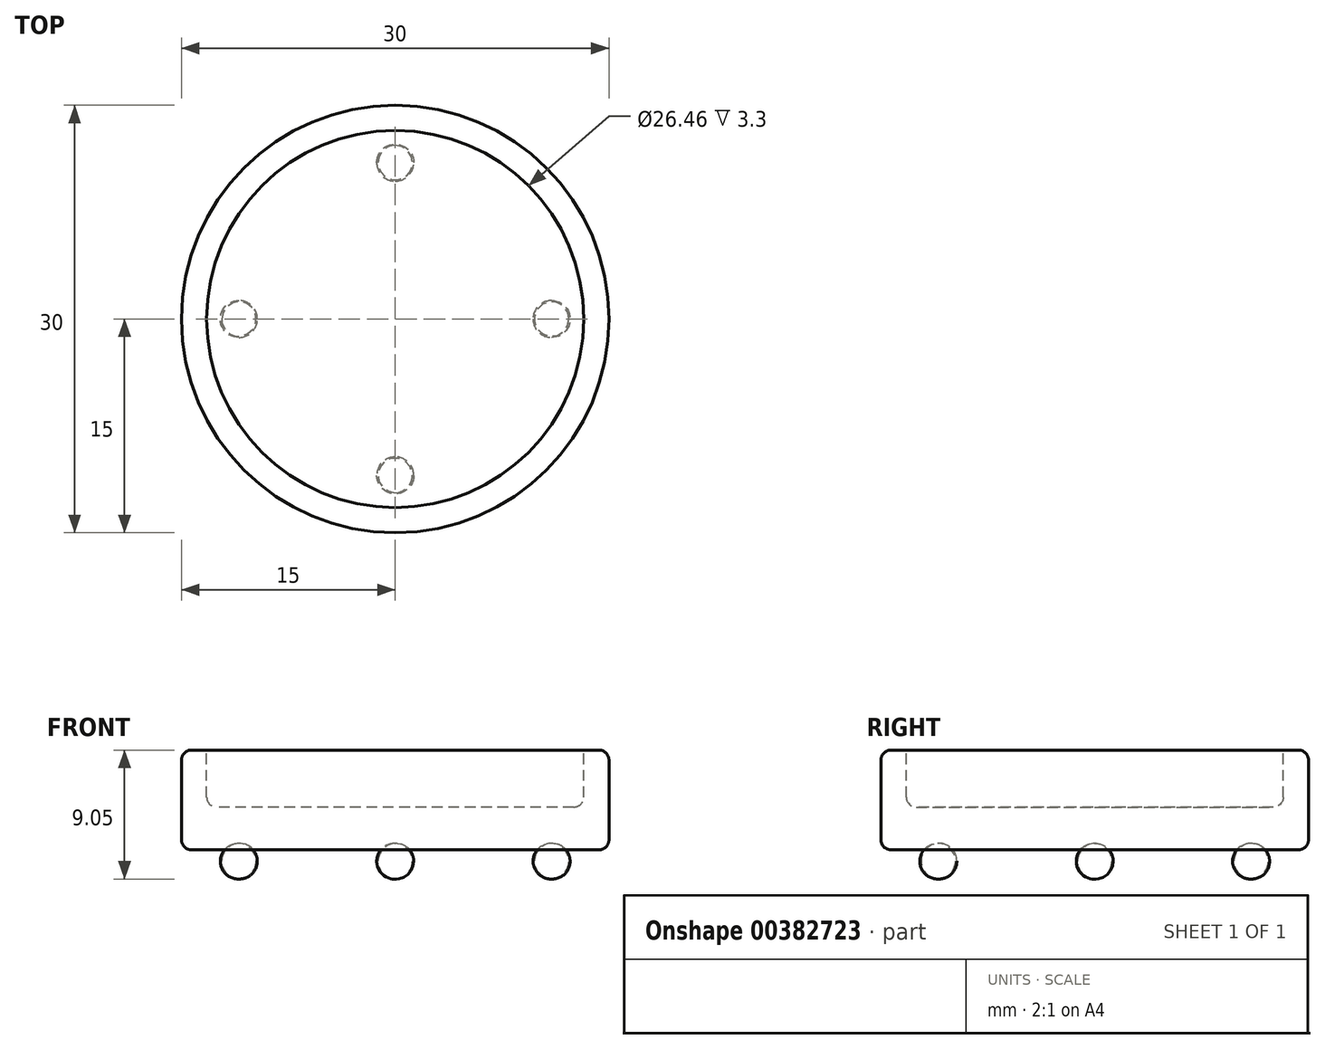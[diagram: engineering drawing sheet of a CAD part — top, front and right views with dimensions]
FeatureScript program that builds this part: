
annotation { "Feature Type Name" : "Feature", "Feature Type Description" : "" }
export const myFeature = defineFeature(function(context is Context, id is Id, definition is map)
    precondition{}
    {
        {
            var Q0;
            Q0=qCreatedBy(makeId("Top.planeOp"),FACE);
            var sketch = newSketch(context, id + "F0", { "sketchPlane" : qUnion([Q0])});
            skCircle(sketch, "E0", {"center": v(0, 0) * mm, "radius": 15 * mm});
            skSolve(sketch);
        }
        {
            var Q0;
            Q0 = qSketchRegion(id + "F0", true);
            extrude(context, id + "F1", {"entities" : qUnion([Q0]), "depth" : 7 * mm});
        }
        {
            var Q0;
            Q0=makeQuery(id+"F1.opExtrude","CAP_FACE",FACE,{"disambiguationData":[OSD([sQuery(id+"F0.wireOp",EDGE,"E0")])],"isStart":false});
            var sketch = newSketch(context, id + "F2", { "sketchPlane" : qUnion([Q0])});
            skCircle(sketch, "E1", {"center": v(0, 0) * mm, "radius": 13.23 * mm});
            skSolve(sketch);
        }
        {
            var Q0;
            Q0=makeQuery(id+"F2.imprint","IMPRINT",FACE,{"disambiguationData":[TD([[makeQuery(id+"F2.imprint","IMPRINT",EDGE,{"derivedFrom":sQuery(id+"F2.wireOp",EDGE,"E1")}),1.0]])]});
            extrude(context, id + "F3", {"entities" : qUnion([Q0]), "operationType" : NewBodyOperationType.REMOVE, "oppositeDirection" : true, "depth" : 4 * mm});
        }
        {
            var Q0;
            Q0=makeQuery(id+"F1.opExtrude","CAP_EDGE",EDGE,{"disambiguationData":[OSD([sQuery(id+"F0.wireOp",EDGE,"E0")])],"isStart":false});
            var Q1;
            Q1=makeQuery(id+"F3.boolean.opBoolean","COPY",EDGE,{"derivedFrom":makeQuery(id+"F3.opExtrude","CAP_EDGE",EDGE,{"disambiguationData":[OSD([sQuery(id+"F2.wireOp",EDGE,"E1")])],"isStart":true})});
            var Q2;
            Q2=makeQuery(id+"F3.boolean.opBoolean","COPY",EDGE,{"derivedFrom":makeQuery(id+"F3.opExtrude","CAP_EDGE",EDGE,{"disambiguationData":[OSD([sQuery(id+"F2.wireOp",EDGE,"E1")])],"isStart":false})});
            var Q3;
            Q3=makeQuery(id+"F1.opExtrude","CAP_FACE",FACE,{"disambiguationData":[OSD([sQuery(id+"F0.wireOp",EDGE,"E0")])],"isStart":true});
            fillet(context, id + "F4", {"entities" : qUnion([Q0, Q1, Q2, Q3]), "radius" : .7 * mm, "tangentPropagation" : true, "allowEdgeOverflow" : false});
        }
        {
            var Q0;
            Q0=makeQuery(id+"F1.opExtrude","CAP_FACE",FACE,{"disambiguationData":[OSD([sQuery(id+"F0.wireOp",EDGE,"E0")])],"isStart":true});
            var sketch = newSketch(context, id + "F5", { "sketchPlane" : qUnion([Q0])});
            skCircle(sketch, "E2", {"center": v(0, 0) * mm, "radius": 10.9 * mm});
            skSolve(sketch);
        }
        {
            var Q0;
            Q0=qCreatedBy(makeId("Front.planeOp"),FACE);
            var sketch = newSketch(context, id + "F6", { "sketchPlane" : qUnion([Q0])});
            skCircle(sketch, "E3", {"center": v(-27.63, 11.5) * mm, "radius": 1.25 * mm});
            skLineSegment(sketch, "E4", {"start": v(-27.71, 14.55) * mm, "end": v(-27.63, 8.1) * mm});
            skSolve(sketch);
        }
        {
            var Q0;
            {var subQ0=sQuery(id+"F6.wireOp",EDGE,"E4");var subQ1=sQuery(id+"F6.wireOp",EDGE,"E3");var subQ2=makeQuery(id+"F6.imprint","INTERSECT",VERTEX,{"disambiguationData":[OD(0.0)],"derivedFrom":[subQ1,subQ0]});Q0=makeQuery(id+"F6.imprint","IMPRINT",FACE,{"disambiguationData":[TD([[makeQuery(id+"F6.imprint","IMPRINT",EDGE,{"disambiguationData":[TD([[subQ2,-1.0]])],"derivedFrom":subQ1}),1.0]])]});}
            var Q1;
            Q1=sQuery(id+"F6.wireOp",EDGE,"E4");
            revolve(context, id + "F7", {"entities" : qUnion([Q0]), "axis" : qUnion([Q1]), "revolveType" : RevolveType.FULL});
        }
        {
            var Q0;
            Q0=makeQuery(id+"F7.opRevolve","SWEPT_BODY",BODY,{"disambiguationData":[OSD([sQuery(id+"F6.wireOp",EDGE,"E3"),sQuery(id+"F6.wireOp",EDGE,"E4")])]});
            transform(context, id + "F8", {"entities" : qUnion([Q0]), "transformType" : TransformType.TRANSLATION_3D, "dx" : 16.7 * mm, "dy" : 0 * mm, "dz" : -12.3 * mm, "makeCopy" : false});
        }
        {
            var Q0;
            Q0=makeQuery(id+"F7.opRevolve","SWEPT_BODY",BODY,{"disambiguationData":[OSD([sQuery(id+"F6.wireOp",EDGE,"E3"),sQuery(id+"F6.wireOp",EDGE,"E4")])]});
            var Q1;
            Q1=sQuery(id+"F5.wireOp",EDGE,"E2");
            circularPattern(context, id + "F9", {"entities" : qUnion([Q0]), "axis" : qUnion([Q1]), "angle" : 360 * degree, "instanceCount" : 4, "equalSpace" : true});
        }
    });
